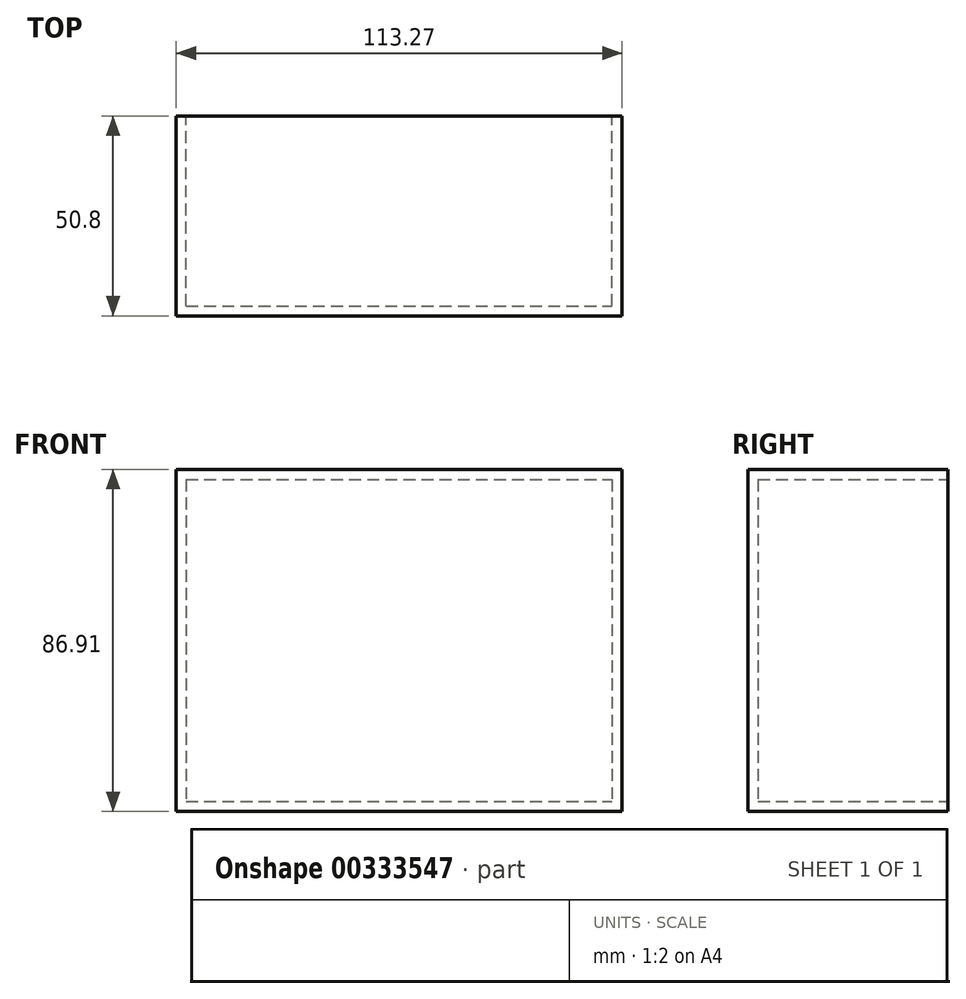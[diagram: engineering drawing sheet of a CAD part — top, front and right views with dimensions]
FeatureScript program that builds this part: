
annotation { "Feature Type Name" : "Feature", "Feature Type Description" : "" }
export const myFeature = defineFeature(function(context is Context, id is Id, definition is map)
    precondition{}
    {
        {
            var Q0;
            Q0=qCreatedBy(makeId("Front.planeOp"),FACE);
            var sketch = newSketch(context, id + "F0", { "sketchPlane" : qUnion([Q0])});
            skLineSegment(sketch, "E0.bottom", {"start": v(-65.73, 55.85) * mm, "end": v(47.54, 55.85) * mm});
            skLineSegment(sketch, "E0.top", {"start": v(-65.73, -31.06) * mm, "end": v(47.54, -31.06) * mm});
            skLineSegment(sketch, "E0.left", {"start": v(-65.73, 55.85) * mm, "end": v(-65.73, -31.06) * mm});
            skLineSegment(sketch, "E0.right", {"start": v(47.54, 55.85) * mm, "end": v(47.54, -31.06) * mm});
            skSolve(sketch);
        }
        {
            var Q0;
            Q0=makeQuery(id+"F0.imprint","IMPRINT",FACE,{"disambiguationData":[TD([[makeQuery(id+"F0.imprint","IMPRINT",EDGE,{"derivedFrom":sQuery(id+"F0.wireOp",EDGE,"E0.bottom")}),-1.0]])]});
            var sketch = newSketch(context, id + "F1", { "sketchPlane" : qUnion([Q0])});
            skLineSegment(sketch, "E1", {"start": v(-66.05, 36.08) * mm, "end": v(46.9, 36.08) * mm});
            skLineSegment(sketch, "E2", {"start": v(-66.05, 16) * mm, "end": v(48.16, 16) * mm});
            skLineSegment(sketch, "E3", {"start": v(-65.73, -5.65) * mm, "end": v(48.16, -5.65) * mm});
            skSolve(sketch);
        }
        {
            var Q0;
            Q0=makeQuery(id+"F0.imprint","IMPRINT",FACE,{"disambiguationData":[TD([[makeQuery(id+"F0.imprint","IMPRINT",EDGE,{"derivedFrom":sQuery(id+"F0.wireOp",EDGE,"E0.bottom")}),-1.0]])]});
            extrude(context, id + "F2", {"entities" : qUnion([Q0]), "depth" : 25.4 * mm});
        }
        {
            var Q0;
            Q0=makeQuery(id+"F2.opExtrude","CAP_FACE",FACE,{"disambiguationData":[OSD([sQuery(id+"F0.wireOp",EDGE,"E0.bottom"),sQuery(id+"F0.wireOp",EDGE,"E0.top"),sQuery(id+"F0.wireOp",EDGE,"E0.left"),sQuery(id+"F0.wireOp",EDGE,"E0.right")])],"isStart":false});
            extrude(context, id + "F3", {"entities" : qUnion([Q0]), "operationType" : NewBodyOperationType.ADD, "depth" : 25.4 * mm});
        }
        {
            var Q0;
            Q0=makeQuery(id+"F2.opExtrude","CAP_FACE",FACE,{"disambiguationData":[OSD([sQuery(id+"F0.wireOp",EDGE,"E0.bottom"),sQuery(id+"F0.wireOp",EDGE,"E0.top"),sQuery(id+"F0.wireOp",EDGE,"E0.left"),sQuery(id+"F0.wireOp",EDGE,"E0.right")])],"isStart":true});
            shell(context, id + "F4", {"entities" : qUnion([Q0]), "thickness" : 2.54 * mm});
        }
        {
            var Q0;
            Q0=sQuery(id+"F1.wireOp",EDGE,"E1");
            extrude(context, id + "F5", {"bodyType" : ToolBodyType.SURFACE, "surfaceEntities" : qUnion([Q0]), "depth" : 49.78 * mm});
        }
        {
            var Q0;
            Q0=makeQuery(id+"F4.opShell","OFFSET_FACE",FACE,{"disambiguationData":[OSD([sQuery(id+"F0.wireOp",EDGE,"E0.bottom"),sQuery(id+"F0.wireOp",EDGE,"E0.top"),sQuery(id+"F0.wireOp",EDGE,"E0.left"),sQuery(id+"F0.wireOp",EDGE,"E0.right")])]});
            var sketch = newSketch(context, id + "F6", { "sketchPlane" : qUnion([Q0])});
            skLineSegment(sketch, "E4", {"start": v(-45, 12.4) * mm, "end": v(63.2, 12.4) * mm});
            skLineSegment(sketch, "E5", {"start": v(-45, -9.1) * mm, "end": v(63.2, -9.1) * mm});
            skSolve(sketch);
        }
        {
            var Q0;
            Q0=sQuery(id+"F6.wireOp",EDGE,"E4");
            extrude(context, id + "F7", {"bodyType" : ToolBodyType.SURFACE, "surfaceEntities" : qUnion([Q0]), "depth" : 48.5 * mm});
        }
        {
            var Q0;
            Q0=makeQuery(id+"F4.opShell","OFFSET_FACE",FACE,{"disambiguationData":[OSD([sQuery(id+"F0.wireOp",EDGE,"E0.bottom"),sQuery(id+"F0.wireOp",EDGE,"E0.top"),sQuery(id+"F0.wireOp",EDGE,"E0.left"),sQuery(id+"F0.wireOp",EDGE,"E0.right")])]});
            var sketch = newSketch(context, id + "F8", { "sketchPlane" : qUnion([Q0])});
            skLineSegment(sketch, "E6", {"start": v(-45, -7.85) * mm, "end": v(63.2, -7.85) * mm});
            skSolve(sketch);
        }
        {
            var Q0;
            Q0=sQuery(id+"F8.wireOp",EDGE,"E6");
            extrude(context, id + "F9", {"bodyType" : ToolBodyType.SURFACE, "surfaceEntities" : qUnion([Q0]), "depth" : 49.53 * mm});
        }
        {
            var Q0;
            Q0=makeQuery(id+"F2.opExtrude","SWEPT_BODY",BODY,{"disambiguationData":[OSD([sQuery(id+"F0.wireOp",EDGE,"E0.bottom"),sQuery(id+"F0.wireOp",EDGE,"E0.top"),sQuery(id+"F0.wireOp",EDGE,"E0.left"),sQuery(id+"F0.wireOp",EDGE,"E0.right")])]});
            var Q1;
            Q1=makeQuery(id+"F9.opExtrude","SWEPT_BODY",BODY,{"disambiguationData":[OSD([sQuery(id+"F8.wireOp",EDGE,"E6")])]});
            var Q2;
            Q2=makeQuery(id+"F5.opExtrude","SWEPT_BODY",BODY,{"disambiguationData":[OSD([sQuery(id+"F1.wireOp",EDGE,"E1")])]});
            var Q3;
            Q3=makeQuery(id+"F7.opExtrude","SWEPT_BODY",BODY,{"disambiguationData":[OSD([sQuery(id+"F6.wireOp",EDGE,"E4")])]});
            var Q4;
            Q4=qCreatedBy(makeId("Origin.pointOp"),VERTEX);
            transform(context, id + "F10", {"entities" : qUnion([Q0, Q1, Q2, Q3]), "transformType" : TransformType.SCALE_UNIFORMLY, "scale" : 1, "scalePoint" : qUnion([Q4]), "makeCopy" : false});
        }
    });
